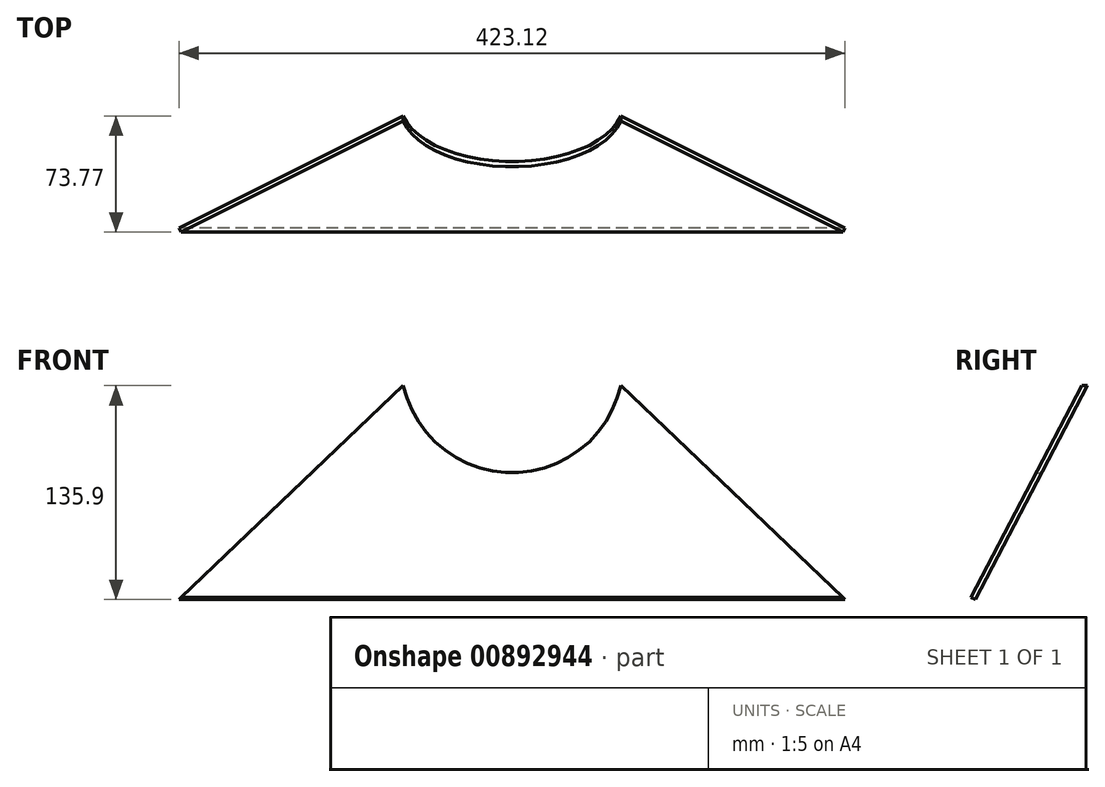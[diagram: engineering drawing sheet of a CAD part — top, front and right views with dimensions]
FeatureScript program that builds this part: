
annotation { "Feature Type Name" : "Feature", "Feature Type Description" : "" }
export const myFeature = defineFeature(function(context is Context, id is Id, definition is map)
    precondition{}
    {
        {
            var Q0;
            Q0=qCreatedBy(makeId("Right.planeOp"),FACE);
            var sketch = newSketch(context, id + "F0", { "sketchPlane" : qUnion([Q0])});
            skLineSegment(sketch, "E0", {"start": v(-109.94, 230) * mm, "end": v(-13.3, 230) * mm, "construction": true});
            skLineSegment(sketch, "E1", {"start": v(-49.53, -25) * mm, "end": v(180.27, -25) * mm, "construction": true});
            skLineSegment(sketch, "E2", {"start": v(180.27, 15) * mm, "end": v(-191.26, 15) * mm, "construction": true});
            skLineSegment(sketch, "E3", {"start": v(-146.7, 80) * mm, "end": v(56.33, 80) * mm, "construction": true});
            skLineSegment(sketch, "E4", {"start": v(-37.5, 230) * mm, "end": v(-150, 15) * mm, "construction": true});
            skLineSegment(sketch, "E5", {"start": v(-101.88, 80) * mm, "end": v(-23.4, 230) * mm});
            skLineSegment(sketch, "E6", {"start": v(-101.88, 80) * mm, "end": v(-99.22, 78.6) * mm});
            skLineSegment(sketch, "E7", {"start": v(-99.22, 78.6) * mm, "end": v(-20, 230) * mm});
            skLineSegment(sketch, "E8", {"start": v(-37.5, 256.26) * mm, "end": v(-37.5, -44.12) * mm, "construction": true});
            skLineSegment(sketch, "E9", {"start": v(-20, 230) * mm, "end": v(-23.4, 230) * mm});
            skSolve(sketch);
        }
        {
            var Q0;
            Q0 = qSketchRegion(id + "F0", true);
            extrude(context, id + "F1", {"entities" : qUnion([Q0]), "endBound" : BoundingType.SYMMETRIC, "depth" : 565 * mm, "offsetDistance" : 25 * mm});
        }
        {
            var Q0;
            Q0=qCreatedBy(makeId("Front.planeOp"),FACE);
            var sketch = newSketch(context, id + "F2", { "sketchPlane" : qUnion([Q0])});
            skCircle(sketch, "E10", {"center": v(0, 230) * mm, "radius": 71 * mm});
            skSolve(sketch);
        }
        {
            var Q0;
            Q0 = qSketchRegion(id + "F2", true);
            extrude(context, id + "F3", {"entities" : qUnion([Q0]), "operationType" : NewBodyOperationType.REMOVE, "endBound" : BoundingType.THROUGH_ALL, "depth" : 25 * mm, "offsetDistance" : 25 * mm});
        }
        {
            var Q0;
            Q0=qCreatedBy(makeId("Front.planeOp"),FACE);
            var sketch = newSketch(context, id + "F4", { "sketchPlane" : qUnion([Q0])});
            skCircle(sketch, "E11", {"center": v(0, 230) * mm, "radius": 71 * mm, "construction": true});
            skLineSegment(sketch, "E12", {"start": v(282.5, 0) * mm, "end": v(282.5, 15) * mm, "construction": true});
            skLineSegment(sketch, "E13", {"start": v(282.5, 15) * mm, "end": v(69.98, 218) * mm, "construction": true});
            skLineSegment(sketch, "E14", {"start": v(69.98, 306.35) * mm, "end": v(408.7, 306.35) * mm});
            skLineSegment(sketch, "E15", {"start": v(408.7, 306.35) * mm, "end": v(408.7, 0) * mm});
            skLineSegment(sketch, "E16", {"start": v(408.7, 0) * mm, "end": v(282.5, 0) * mm});
            skLineSegment(sketch, "E17", {"start": v(69.29, 214.5) * mm, "end": v(275.74, 17.3) * mm});
            skLineSegment(sketch, "E18", {"start": v(275.74, 17.3) * mm, "end": v(275.74, 0) * mm});
            skLineSegment(sketch, "E19", {"start": v(282.5, 0) * mm, "end": v(275.74, 0) * mm});
            skLineSegment(sketch, "E20", {"start": v(69.29, 214.5) * mm, "end": v(69.29, 271.22) * mm});
            skLineSegment(sketch, "E21", {"start": v(69.29, 271.22) * mm, "end": v(69.29, 306.35) * mm});
            skLineSegment(sketch, "E22", {"start": v(69.29, 306.35) * mm, "end": v(69.98, 306.35) * mm});
            skLineSegment(sketch, "E23.MirrorCS", {"start": v(-69.29, 306.35) * mm, "end": v(-69.98, 306.35) * mm});
            skLineSegment(sketch, "E24.MirrorCS", {"start": v(-282.5, 0) * mm, "end": v(-275.74, 0) * mm});
            skLineSegment(sketch, "E25.MirrorCS", {"start": v(-282.5, 0) * mm, "end": v(-282.5, 15) * mm, "construction": true});
            skLineSegment(sketch, "E26.MirrorCS", {"start": v(-275.74, 17.3) * mm, "end": v(-275.74, 0) * mm});
            skLineSegment(sketch, "E27.MirrorCS", {"start": v(-282.5, 15) * mm, "end": v(-69.98, 218) * mm, "construction": true});
            skLineSegment(sketch, "E28.MirrorCS", {"start": v(-69.29, 214.5) * mm, "end": v(-275.74, 17.3) * mm});
            skLineSegment(sketch, "E29.MirrorCS", {"start": v(-408.7, 0) * mm, "end": v(-282.5, 0) * mm});
            skLineSegment(sketch, "E30.MirrorCS", {"start": v(-69.29, 271.22) * mm, "end": v(-69.29, 306.35) * mm});
            skLineSegment(sketch, "E31.MirrorCS", {"start": v(-69.98, 306.35) * mm, "end": v(-408.7, 306.35) * mm});
            skLineSegment(sketch, "E32.MirrorCS", {"start": v(-69.29, 214.5) * mm, "end": v(-69.29, 271.22) * mm});
            skLineSegment(sketch, "E33.MirrorCS", {"start": v(-408.7, 306.35) * mm, "end": v(-408.7, 0) * mm});
            skSolve(sketch);
        }
        {
            var Q0;
            Q0 = qSketchRegion(id + "F4", true);
            extrude(context, id + "F5", {"entities" : qUnion([Q0]), "operationType" : NewBodyOperationType.REMOVE, "endBound" : BoundingType.THROUGH_ALL, "depth" : 25 * mm, "offsetDistance" : 25 * mm});
        }
    });
